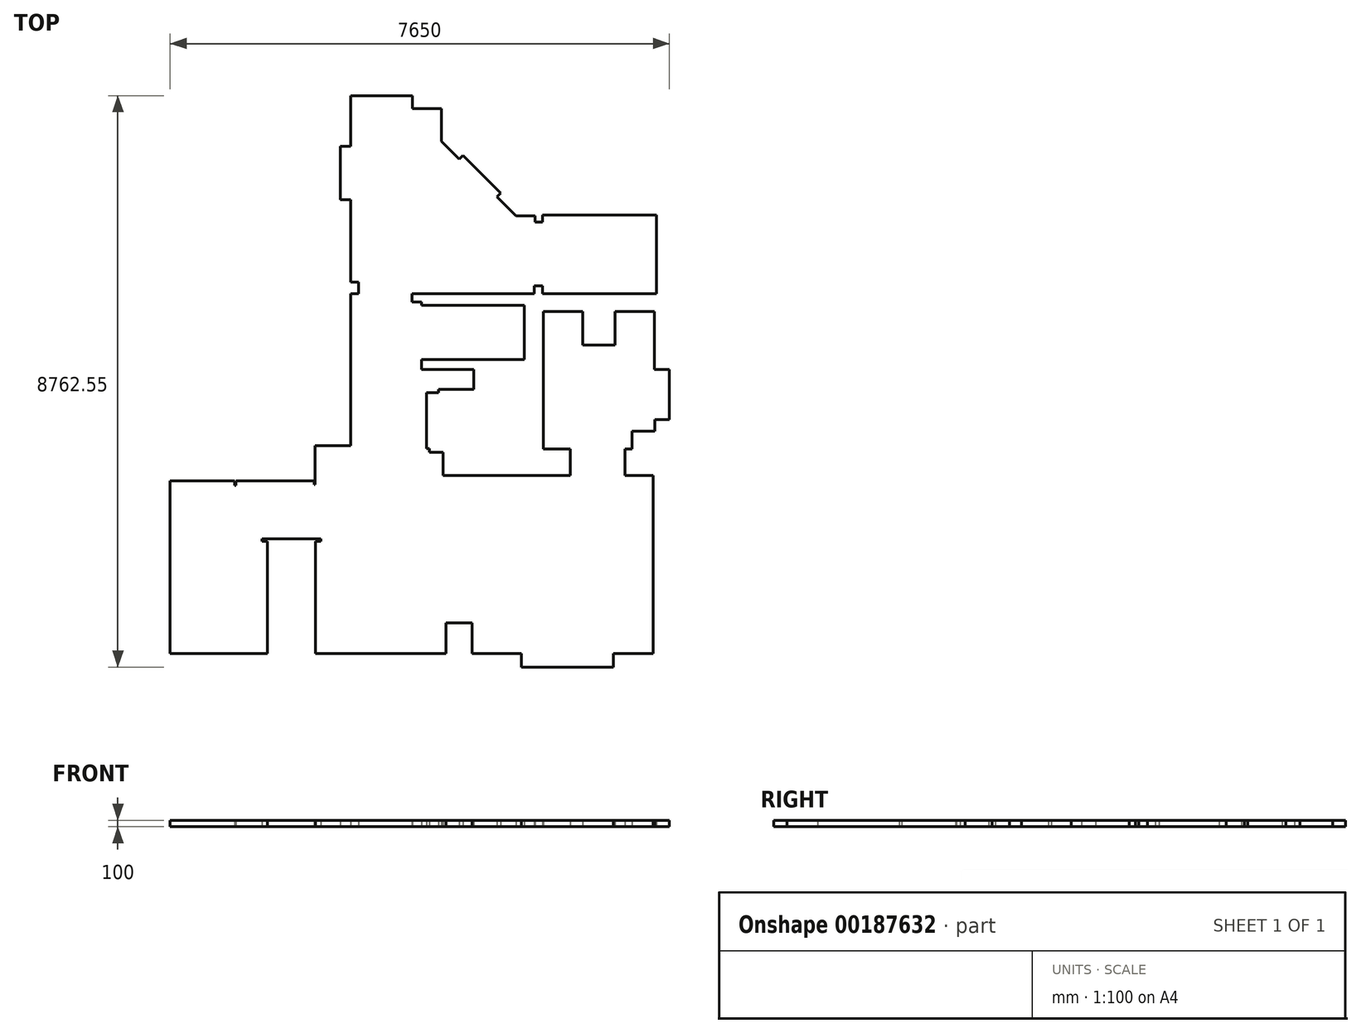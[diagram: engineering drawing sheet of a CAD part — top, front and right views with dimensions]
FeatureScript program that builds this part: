
annotation { "Feature Type Name" : "Feature", "Feature Type Description" : "" }
export const myFeature = defineFeature(function(context is Context, id is Id, definition is map)
    precondition{}
    {
        {
            var Q0;
            Q0=qCreatedBy(makeId("Top.planeOp"),FACE);
            var sketch = newSketch(context, id + "F0", { "sketchPlane" : qUnion([Q0])});
            skLineSegment(sketch, "E0", {"start": v(4125, 3880) * mm, "end": v(3525, 3880) * mm});
            skLineSegment(sketch, "E1", {"start": v(3525, 3880) * mm, "end": v(3525, 3365) * mm});
            skLineSegment(sketch, "E2", {"start": v(3525, 3365) * mm, "end": v(3025, 3365) * mm});
            skLineSegment(sketch, "E3", {"start": v(3025, 3365) * mm, "end": v(3025, 3880) * mm});
            skLineSegment(sketch, "E4", {"start": v(3025, 3880) * mm, "end": v(2425, 3880) * mm});
            skLineSegment(sketch, "E5", {"start": v(2425, 3880) * mm, "end": v(2425, 1775) * mm});
            skLineSegment(sketch, "E6", {"start": v(2425, 1775) * mm, "end": v(2835, 1775) * mm});
            skLineSegment(sketch, "E7", {"start": v(2835, 1775) * mm, "end": v(2835, 1365) * mm});
            skLineSegment(sketch, "E8", {"start": v(2835, 1365) * mm, "end": v(885, 1365) * mm});
            skLineSegment(sketch, "E9", {"start": v(885, 1365) * mm, "end": v(885, 1725) * mm});
            skLineSegment(sketch, "E10", {"start": v(885, 1725) * mm, "end": v(680, 1725) * mm});
            skLineSegment(sketch, "E11", {"start": v(680, 1725) * mm, "end": v(680, 1780) * mm});
            skLineSegment(sketch, "E12", {"start": v(680, 1780) * mm, "end": v(630, 1780) * mm});
            skLineSegment(sketch, "E13", {"start": v(630, 1780) * mm, "end": v(630, 2640) * mm});
            skLineSegment(sketch, "E14", {"start": v(630, 2640) * mm, "end": v(815, 2640) * mm});
            skLineSegment(sketch, "E15", {"start": v(815, 2640) * mm, "end": v(815, 2685) * mm});
            skLineSegment(sketch, "E16", {"start": v(815, 2685) * mm, "end": v(1355, 2685) * mm});
            skLineSegment(sketch, "E17", {"start": v(1355, 2685) * mm, "end": v(1355, 2995) * mm});
            skLineSegment(sketch, "E18", {"start": v(1355, 2995) * mm, "end": v(560, 2995) * mm});
            skLineSegment(sketch, "E19", {"start": v(560, 2995) * mm, "end": v(560, 3145) * mm});
            skLineSegment(sketch, "E20", {"start": v(560, 3145) * mm, "end": v(2130, 3145) * mm});
            skLineSegment(sketch, "E21", {"start": v(2130, 3145) * mm, "end": v(2130, 3975) * mm});
            skLineSegment(sketch, "E22", {"start": v(2130, 3975) * mm, "end": v(560, 3975) * mm});
            skLineSegment(sketch, "E23", {"start": v(560, 3975) * mm, "end": v(560, 4025) * mm});
            skLineSegment(sketch, "E24", {"start": v(560, 4025) * mm, "end": v(410, 4025) * mm});
            skLineSegment(sketch, "E25", {"start": v(410, 4025) * mm, "end": v(410, 4155) * mm});
            skLineSegment(sketch, "E26", {"start": v(-530, 4155) * mm, "end": v(-530, 1825) * mm});
            skLineSegment(sketch, "E27", {"start": v(-530, 1825) * mm, "end": v(-1075, 1825) * mm});
            skLineSegment(sketch, "E28", {"start": v(-1075, 1825) * mm, "end": v(-1075, 1230) * mm});
            skLineSegment(sketch, "E29", {"start": v(-1075, 1230) * mm, "end": v(-1090, 1230) * mm});
            skLineSegment(sketch, "E30", {"start": v(-1090, 1230) * mm, "end": v(-1090, 1285) * mm});
            skLineSegment(sketch, "E31", {"start": v(-1090, 1285) * mm, "end": v(-2290, 1285) * mm});
            skLineSegment(sketch, "E32", {"start": v(-2290, 1285) * mm, "end": v(-2290, 1215) * mm});
            skLineSegment(sketch, "E33", {"start": v(-2290, 1215) * mm, "end": v(-2305, 1215) * mm});
            skLineSegment(sketch, "E34", {"start": v(-2305, 1215) * mm, "end": v(-2305, 1285) * mm});
            skLineSegment(sketch, "E35", {"start": v(-2305, 1285) * mm, "end": v(-3295, 1285) * mm});
            skLineSegment(sketch, "E36", {"start": v(-3295, 1285) * mm, "end": v(-3295, -1365) * mm});
            skLineSegment(sketch, "E37", {"start": v(-3295, -1365) * mm, "end": v(-1805, -1365) * mm});
            skLineSegment(sketch, "E38", {"start": v(-1805, -1365) * mm, "end": v(-1805, 355) * mm});
            skLineSegment(sketch, "E39", {"start": v(-1805, 355) * mm, "end": v(-1885, 355) * mm});
            skLineSegment(sketch, "E40", {"start": v(-1885, 355) * mm, "end": v(-1885, 393) * mm});
            skLineSegment(sketch, "E41", {"start": v(-1885, 393) * mm, "end": v(-985, 393) * mm});
            skLineSegment(sketch, "E42", {"start": v(-985, 393) * mm, "end": v(-985, 355) * mm});
            skLineSegment(sketch, "E43", {"start": v(-985, 355) * mm, "end": v(-1070, 355) * mm});
            skLineSegment(sketch, "E44", {"start": v(-1070, 355) * mm, "end": v(-1070, -1365) * mm});
            skLineSegment(sketch, "E45", {"start": v(-1070, -1365) * mm, "end": v(930, -1365) * mm});
            skLineSegment(sketch, "E46", {"start": v(930, -1365) * mm, "end": v(930, -895) * mm});
            skLineSegment(sketch, "E47", {"start": v(930, -895) * mm, "end": v(1335, -895) * mm});
            skLineSegment(sketch, "E48", {"start": v(1335, -895) * mm, "end": v(1335, -1365) * mm});
            skLineSegment(sketch, "E49", {"start": v(1335, -1365) * mm, "end": v(2090, -1365) * mm});
            skLineSegment(sketch, "E50", {"start": v(2090, -1365) * mm, "end": v(2090, -1570) * mm});
            skLineSegment(sketch, "E51", {"start": v(2090, -1570) * mm, "end": v(3500, -1570) * mm});
            skLineSegment(sketch, "E52", {"start": v(3500, -1570) * mm, "end": v(3500, -1365) * mm});
            skLineSegment(sketch, "E53", {"start": v(3500, -1365) * mm, "end": v(4105, -1365) * mm});
            skLineSegment(sketch, "E54", {"start": v(4105, -1365) * mm, "end": v(4105, 1365) * mm});
            skLineSegment(sketch, "E55", {"start": v(4105, 1365) * mm, "end": v(3675, 1365) * mm});
            skLineSegment(sketch, "E56", {"start": v(3675, 1365) * mm, "end": v(3675, 1775) * mm});
            skLineSegment(sketch, "E57", {"start": v(3675, 1775) * mm, "end": v(3780, 1775) * mm});
            skLineSegment(sketch, "E58", {"start": v(3780, 1775) * mm, "end": v(3780, 2045) * mm});
            skLineSegment(sketch, "E59", {"start": v(3780, 2045) * mm, "end": v(4135, 2045) * mm});
            skLineSegment(sketch, "E60", {"start": v(4135, 2045) * mm, "end": v(4135, 2225) * mm});
            skLineSegment(sketch, "E61", {"start": v(4135, 2225) * mm, "end": v(4355, 2225) * mm});
            skLineSegment(sketch, "E62", {"start": v(4355, 2225) * mm, "end": v(4355, 2990) * mm});
            skLineSegment(sketch, "E63", {"start": v(4355, 2990) * mm, "end": v(4125, 2990) * mm});
            skLineSegment(sketch, "E64", {"start": v(4125, 2990) * mm, "end": v(4125, 3880) * mm});
            skLineSegment(sketch, "E65", {"start": v(-530, 4155) * mm, "end": v(-410, 4155) * mm});
            skLineSegment(sketch, "E66", {"start": v(-410, 4155) * mm, "end": v(-410, 4332.55) * mm});
            skLineSegment(sketch, "E67", {"start": v(-410, 4332.55) * mm, "end": v(-530, 4332.55) * mm});
            skLineSegment(sketch, "E68", {"start": v(-530, 4332.55) * mm, "end": v(-530, 5597.55) * mm});
            skLineSegment(sketch, "E69", {"start": v(-530, 5597.55) * mm, "end": v(-685, 5597.55) * mm});
            skLineSegment(sketch, "E70", {"start": v(-685, 5597.55) * mm, "end": v(-685, 6412.55) * mm});
            skLineSegment(sketch, "E71", {"start": v(-685, 6412.55) * mm, "end": v(-530, 6412.55) * mm});
            skLineSegment(sketch, "E72", {"start": v(-530, 6412.55) * mm, "end": v(-530, 7192.55) * mm});
            skLineSegment(sketch, "E73", {"start": v(-530, 7192.55) * mm, "end": v(420, 7192.55) * mm});
            skLineSegment(sketch, "E74", {"start": v(420, 7192.55) * mm, "end": v(420, 6992.55) * mm});
            skLineSegment(sketch, "E75", {"start": v(420, 6992.55) * mm, "end": v(860, 6992.55) * mm});
            skLineSegment(sketch, "E76", {"start": v(860, 6992.55) * mm, "end": v(860, 6492.55) * mm});
            skLineSegment(sketch, "E77", {"start": v(860, 6492.55) * mm, "end": v(1132.24, 6220.31) * mm});
            skLineSegment(sketch, "E78", {"start": v(1132.24, 6220.31) * mm, "end": v(1188.8, 6276.88) * mm});
            skLineSegment(sketch, "E79", {"start": v(1188.8, 6276.88) * mm, "end": v(1768.63, 5697.05) * mm});
            skLineSegment(sketch, "E80", {"start": v(1768.63, 5697.05) * mm, "end": v(1712.06, 5640.48) * mm});
            skLineSegment(sketch, "E81", {"start": v(1712.06, 5640.48) * mm, "end": v(2001.98, 5350.57) * mm});
            skLineSegment(sketch, "E82", {"start": v(2001.98, 5350.57) * mm, "end": v(2296.98, 5350.57) * mm});
            skLineSegment(sketch, "E83", {"start": v(4156.98, 4155) * mm, "end": v(2411.98, 4155) * mm});
            skLineSegment(sketch, "E84", {"start": v(2411.98, 4155) * mm, "end": v(2411.98, 4275) * mm});
            skLineSegment(sketch, "E85", {"start": v(2411.98, 4275) * mm, "end": v(2281.98, 4275) * mm});
            skLineSegment(sketch, "E86", {"start": v(2281.98, 4275) * mm, "end": v(2281.98, 4155) * mm});
            skLineSegment(sketch, "E87", {"start": v(2281.98, 4155) * mm, "end": v(410, 4155) * mm});
            skLineSegment(sketch, "E88", {"start": v(2296.98, 5350.57) * mm, "end": v(2296.98, 5255.57) * mm});
            skLineSegment(sketch, "E89", {"start": v(2296.98, 5255.57) * mm, "end": v(2411.98, 5255.57) * mm});
            skLineSegment(sketch, "E90", {"start": v(2411.98, 5255.57) * mm, "end": v(2411.98, 5360.57) * mm});
            skLineSegment(sketch, "E91", {"start": v(2411.98, 5360.57) * mm, "end": v(4156.98, 5360.57) * mm});
            skLineSegment(sketch, "E92", {"start": v(4156.98, 5360.57) * mm, "end": v(4156.98, 4155) * mm});
            skSolve(sketch);
        }
        {
            var Q0;
            Q0 = qSketchRegion(id + "F0", true);
            extrude(context, id + "F1", {"entities" : qUnion([Q0]), "depth" : 100 * mm});
        }
    });
